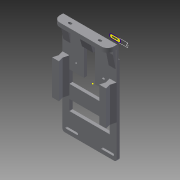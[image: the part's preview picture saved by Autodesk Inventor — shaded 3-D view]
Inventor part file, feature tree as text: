
AUTODESK INVENTOR PART (.ipt)
format: ipt  version: 2015 (Build 190159000, 159)  size: 432,640 bytes
history: native  units: mm
features: extrude x19, sketch x18, mirror x4, projected_geometry x4, fillet x3, chamfer x3
ambient origin geometry x8: Origin, YZ Plane, XZ Plane, XY Plane, X Axis, Y Axis, Z Axis, Center Point
bodies: 实体1 (feature_tree)
feature tree (51):
  sketch  "草图1"  dims[d0=6.4mm d1=3.2mm d2=42.5mm d7=3.2mm]
  extrude  "拉伸1"  Depth=3.2mm
  fillet  "圆角1"  Radius=42.5mm
  fillet  "圆角2"  Radius=3.2mm
  extrude  "拉伸2"  Depth=18.67mm
  sketch  "草图2"  dims[d8=19.7mm d9=18.67mm]
  extrude  "拉伸4"  Depth=2.0mm
  mirror  "镜像1"
  extrude  "拉伸5"  Depth=2.5mm
  extrude  "拉伸6"  Depth=38.0mm
  extrude  "拉伸9"  Depth=3.3mm
  sketch  "草图7"  dims[d23=3.3mm d24=32.25mm]
  extrude  "拉伸10"  Depth=39.0mm
  mirror  "镜像4"
  extrude  "拉伸11"  Depth=3.0mm
  extrude  "拉伸12"  Depth=4.5mm TaperAngle=0.0deg
  mirror  "镜像5"
  extrude  "拉伸13"  Depth=3.0mm
  sketch  "草图11"  dims[d33=3.0mm d34=3.0mm]
  extrude  "拉伸14"  Depth=6.0mm
  extrude  "拉伸15"  Depth=2.0mm TaperAngle=0.0deg
  extrude  "拉伸16"  Depth=9.0mm
  sketch  "草图15"  dims[d45=35.0mm d46=2.0mm]
  extrude  "拉伸17"  Depth=2.0mm
  extrude  "拉伸18"  Depth=7.5mm
  extrude  "拉伸19"  Depth=1.5mm
  chamfer  "倒角1"  Distance=1.0mm
  fillet  "圆角3"  Radius=106.0mm
  extrude  "拉伸20"  Depth=50.0mm
  extrude  "拉伸21"  Depth=10.0mm
  extrude  "拉伸22"  Depth=15.0mm TaperAngle=0.0deg
  chamfer  "倒角2"  Distance=2.0mm
  mirror  "镜像6"
  chamfer  "倒角3"  Distance=7.5mm
  sketch  "草图3"  dims[d10=4.0mm d14=2.0mm]
  sketch  "草图4"  dims[d15=2.5mm d16=39.4mm]
  sketch  "草图5"  dims[d18=90.0mm d19=38.0mm d20=45.0mm]
  sketch  "草图8"  dims[d25=10.0mm d26=39.0mm]
  projected_geometry  "投影回路2"
  sketch  "草图9"  dims[d27=16.0mm d28=3.0mm]
  projected_geometry  "投影回路3"
  sketch  "草图10"  dims[d30=26.0mm d31=4.5mm d32=0.0mm]
  projected_geometry  "投影回路4"
  projected_geometry  "投影回路5"
  sketch  "草图12"  dims[d35=2.6mm d36=0.0mm d37=6.0mm]
  sketch  "草图13"  dims[d40=5.2mm d41=2.0mm d42=0.0mm]
  sketch  "草图14"  dims[d43=70.0mm d44=9.0mm]
  sketch  "草图16"  dims[d47=15.0mm d48=7.5mm]
  sketch  "草图17"  dims[d49=2.5mm d50=0.0mm d51=1.5mm]
  sketch  "草图18"  dims[d52=1.5mm]
  sketch  "草图19"  dims[d53=6.0mm d54=1.0mm d55=0.0mm d56=106.0mm d57=50.0mm d67=10.0mm d69=15.0mm d70=0.0mm d71=2.0mm d72=7.5mm d73=2.0mm d74=7.5mm d75=15.0mm d76=0.0mm d77=15.0mm d78=0.0mm d79=2.0mm d80=7.5mm d81=7.5mm d82=2.0mm d83=15.0mm d84=0.0mm d85=2.5mm d86=4.35mm d88=2.0mm d89=0.0mm d90=11.0mm d91=10.0mm d92=0.0mm d93=10.0mm d94=0.0mm d95=6.0mm d96=13.0mm d97=0.0mm d100=1.6mm d102=6.2mm d103=22.6mm d104=1.6mm d105=3.1mm d106=3.5mm d107=2.0mm d108=2.0mm d109=0.0mm d110=2.0mm d111=0.0mm d112=16.0mm d113=32.0mm d114=8.0mm d115=12.0mm d116=0.0mm d117=25.0mm d118=7.0mm d119=45.0deg d120=9.0mm d121=10.0mm d122=10.0mm d123=15.0mm d124=18.0mm d125=31.0mm d126=31.0mm d127=79.0mm d128=10.0mm d129=0.0mm d130=1.5mm d131=20.0mm d132=10.0mm d133=0.0mm d134=10.0mm d135=4.0mm d136=25.0mm d137=0.0mm d138=4.0mm d139=20.0mm d140=45.0deg d141=2.0mm d142=20.0mm d143=45.0deg]
